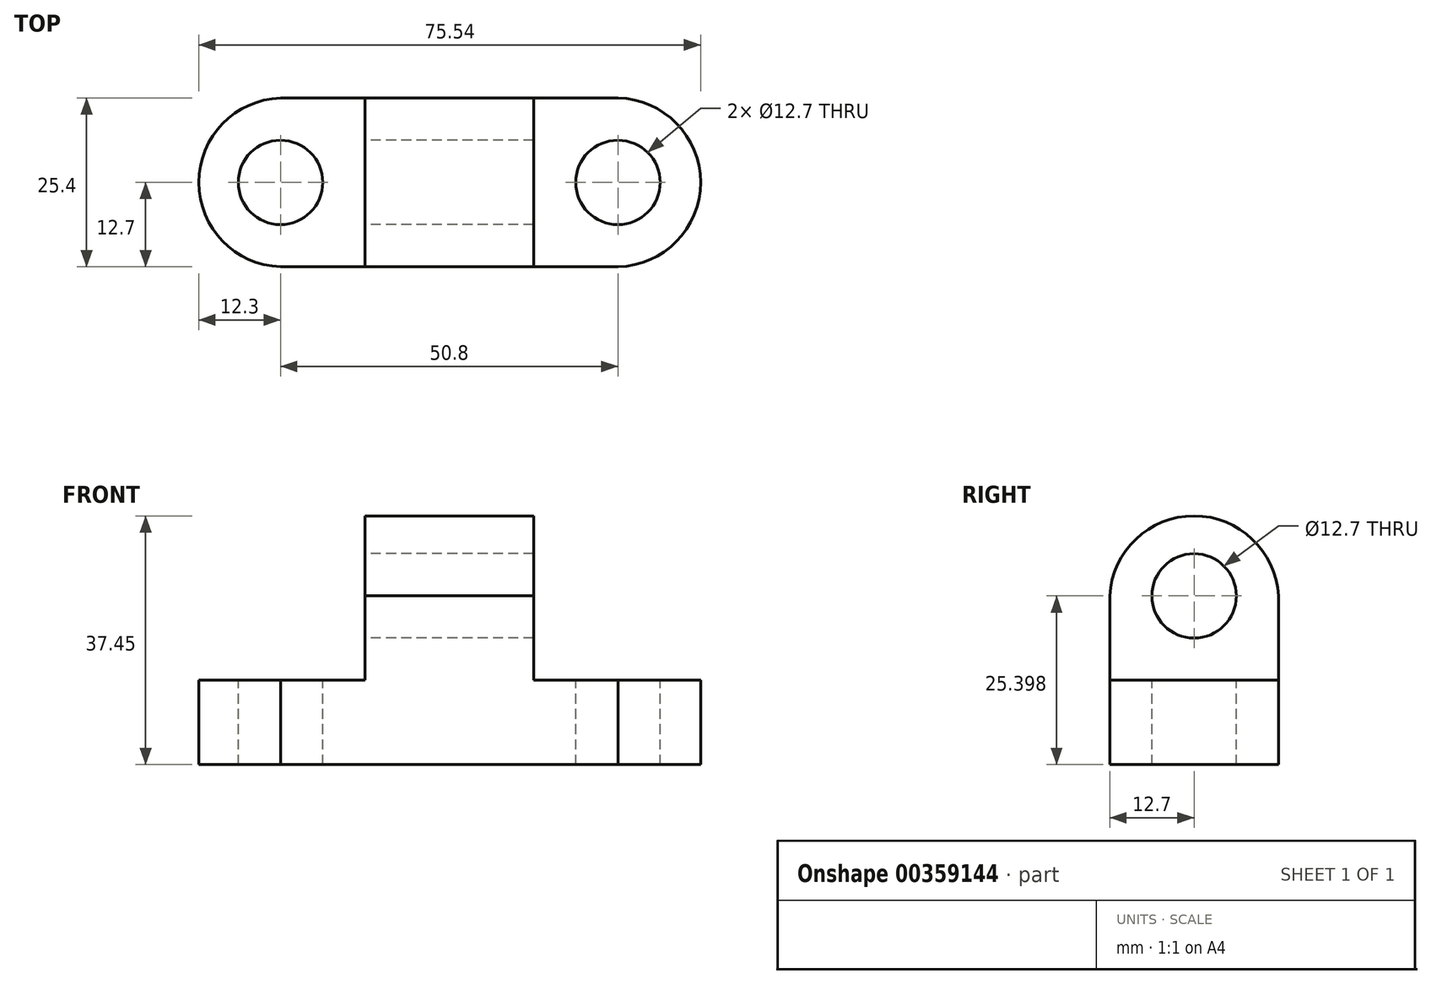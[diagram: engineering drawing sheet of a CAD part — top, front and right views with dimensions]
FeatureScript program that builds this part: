
annotation { "Feature Type Name" : "Feature", "Feature Type Description" : "" }
export const myFeature = defineFeature(function(context is Context, id is Id, definition is map)
    precondition{}
    {
        {
            var Q0;
            Q0=qCreatedBy(makeId("Front.planeOp"),FACE);
            var sketch = newSketch(context, id + "F0", { "sketchPlane" : qUnion([Q0])});
            skLineSegment(sketch, "E0", {"start": v(-42.17, 14.05) * mm, "end": v(-16.77, 14.05) * mm});
            skLineSegment(sketch, "E1", {"start": v(-16.77, 14.05) * mm, "end": v(-16.77, 39.45) * mm});
            skLineSegment(sketch, "E2", {"start": v(-16.77, 39.45) * mm, "end": v(8.63, 39.45) * mm});
            skLineSegment(sketch, "E3", {"start": v(8.63, 39.45) * mm, "end": v(8.63, 14.05) * mm});
            skLineSegment(sketch, "E4", {"start": v(8.63, 14.05) * mm, "end": v(34.03, 14.05) * mm});
            skLineSegment(sketch, "E5", {"start": v(34.03, 14.05) * mm, "end": v(34.03, 1.35) * mm});
            skLineSegment(sketch, "E6", {"start": v(34.03, 1.35) * mm, "end": v(-42.17, 1.35) * mm});
            skLineSegment(sketch, "E7", {"start": v(-42.17, 1.35) * mm, "end": v(-42.17, 14.05) * mm});
            skSolve(sketch);
        }
        {
            var Q0;
            Q0 = qSketchRegion(id + "F0", true);
            extrude(context, id + "F1", {"entities" : qUnion([Q0]), "depth" : 25.4 * mm});
        }
        {
            var Q0;
            Q0=makeQuery(id+"F1.opExtrude","SWEPT_FACE",FACE,{"disambiguationData":[OSD([sQuery(id+"F0.wireOp",EDGE,"E1")])]});
            var sketch = newSketch(context, id + "F2", { "sketchPlane" : qUnion([Q0])});
            skCircle(sketch, "E8", {"center": v(12.7, 26.75) * mm, "radius": 6.35 * mm});
            skArc(sketch, "E9", {"start": v(25.4, 26.75) * mm, "mid": v(12.7, 38.8) * mm, "end": v(0, 26.75) * mm});
            skSolve(sketch);
        }
        {
            var Q0;
            Q0 = qSketchRegion(id + "F2", true);
            var Q1;
            {var subQ0=sQuery(id+"F2.wireOp",EDGE,"E9");Q1=makeQuery(id+"F2.imprint","IMPRINT",FACE,{"disambiguationData":[TD([[makeQuery(id+"F2.imprint","IMPRINT",EDGE,{"derivedFrom":subQ0}),-1.0]])]});}
            extrude(context, id + "F3", {"entities" : qUnion([Q0, Q1]), "operationType" : NewBodyOperationType.REMOVE, "oppositeDirection" : true, "depth" : 25.4 * mm});
        }
        {
            var Q0;
            Q0=makeQuery(id+"F1.opExtrude","SWEPT_FACE",FACE,{"disambiguationData":[OSD([sQuery(id+"F0.wireOp",EDGE,"E0")])]});
            var sketch = newSketch(context, id + "F4", { "sketchPlane" : qUnion([Q0])});
            skCircle(sketch, "E10", {"center": v(-29.47, -12.7) * mm, "radius": 6.35 * mm});
            skArc(sketch, "E11", {"start": v(-29.47, 0) * mm, "mid": v(-41.77, -12.7) * mm, "end": v(-29.47, -25.4) * mm});
            skSolve(sketch);
        }
        {
            var Q0;
            Q0 = qSketchRegion(id + "F4", true);
            var Q1;
            {var subQ0=sQuery(id+"F4.wireOp",EDGE,"E11");Q1=makeQuery(id+"F4.imprint","IMPRINT",FACE,{"disambiguationData":[TD([[makeQuery(id+"F4.imprint","IMPRINT",EDGE,{"derivedFrom":subQ0}),-1.0]])]});}
            extrude(context, id + "F5", {"entities" : qUnion([Q0, Q1]), "operationType" : NewBodyOperationType.REMOVE, "oppositeDirection" : true, "depth" : 25.4 * mm});
        }
        {
            var Q0;
            Q0=makeQuery(id+"F1.opExtrude","SWEPT_FACE",FACE,{"disambiguationData":[OSD([sQuery(id+"F0.wireOp",EDGE,"E4")])]});
            var sketch = newSketch(context, id + "F6", { "sketchPlane" : qUnion([Q0])});
            skCircle(sketch, "E12", {"center": v(21.33, -12.7) * mm, "radius": 6.35 * mm});
            skArc(sketch, "E13", {"start": v(21.33, -25.4) * mm, "mid": v(33.77, -12.7) * mm, "end": v(21.33, 0) * mm});
            skSolve(sketch);
        }
        {
            var Q0;
            Q0 = qSketchRegion(id + "F6", true);
            var Q1;
            {var subQ0=sQuery(id+"F6.wireOp",EDGE,"E13");Q1=makeQuery(id+"F6.imprint","IMPRINT",FACE,{"disambiguationData":[TD([[makeQuery(id+"F6.imprint","IMPRINT",EDGE,{"derivedFrom":subQ0}),-1.0]])]});}
            extrude(context, id + "F7", {"entities" : qUnion([Q0, Q1]), "operationType" : NewBodyOperationType.REMOVE, "oppositeDirection" : true, "depth" : 25.4 * mm});
        }
    });
